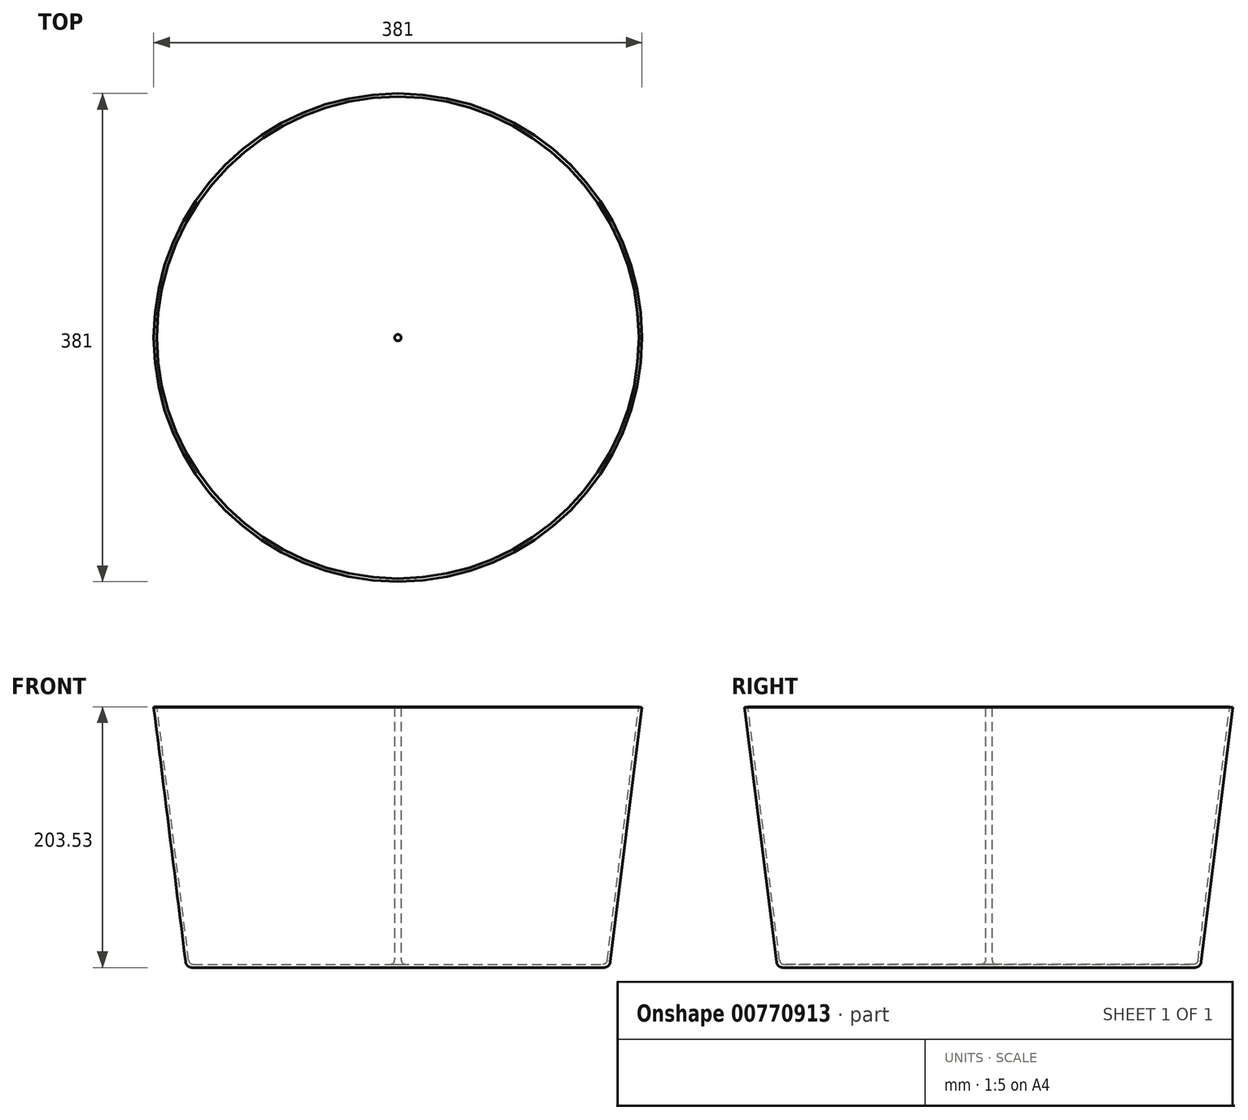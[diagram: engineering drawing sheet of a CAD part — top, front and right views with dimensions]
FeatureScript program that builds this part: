
annotation { "Feature Type Name" : "Feature", "Feature Type Description" : "" }
export const myFeature = defineFeature(function(context is Context, id is Id, definition is map)
    precondition{}
    {
        {
            var Q0;
            Q0=qCreatedBy(makeId("Front.planeOp"),FACE);
            var sketch = newSketch(context, id + "F0", { "sketchPlane" : qUnion([Q0])});
            skLineSegment(sketch, "E0", {"start": v(0, 0) * mm, "end": v(160.73, 0) * mm});
            skLineSegment(sketch, "E1", {"start": v(0, 0) * mm, "end": v(0, 203.21) * mm});
            skLineSegment(sketch, "E2", {"start": v(165.64, 4.34) * mm, "end": v(190.5, 203.21) * mm});
            skLineSegment(sketch, "E3.0", {"start": v(163.23, 5.54) * mm, "end": v(187.98, 203.53) * mm});
            skLineSegment(sketch, "E3.1", {"start": v(5.97, 2.54) * mm, "end": v(159.83, 2.54) * mm});
            skLineSegment(sketch, "E3.2", {"start": v(2.54, 5.97) * mm, "end": v(2.54, 203.21) * mm});
            skPoint(sketch, "E4.visualSharp", {"position": v(165.1, 0) * mm});
            skArc(sketch, "E4.filletArc", {"start": v(160.73, 0) * mm, "mid": v(164, 1.24) * mm, "end": v(165.64, 4.34) * mm});
            skArc(sketch, "E5.filletArc", {"start": v(159.83, 2.54) * mm, "mid": v(162.1, 3.4) * mm, "end": v(163.23, 5.54) * mm});
            skPoint(sketch, "E6.visualSharp", {"position": v(2.54, 2.54) * mm});
            skArc(sketch, "E6.filletArc", {"start": v(2.54, 5.97) * mm, "mid": v(3.54, 3.54) * mm, "end": v(5.97, 2.54) * mm});
            skLineSegment(sketch, "E7", {"start": v(0, 203.21) * mm, "end": v(2.54, 203.21) * mm});
            skLineSegment(sketch, "E8", {"start": v(187.98, 203.53) * mm, "end": v(190.5, 203.21) * mm});
            skLineSegment(sketch, "E9", {"start": v(187.98, 203.53) * mm, "end": v(2.54, 203.21) * mm});
            skSolve(sketch);
        }
        {
            var Q0;
            Q0=makeQuery(id+"F0.imprint","IMPRINT",FACE,{"disambiguationData":[TD([[makeQuery(id+"F0.imprint","IMPRINT",EDGE,{"derivedFrom":sQuery(id+"F0.wireOp",EDGE,"E0")}),1.0]])]});
            var Q1;
            Q1=sQuery(id+"F0.wireOp",EDGE,"E1");
            revolve(context, id + "F1", {"surfaceOperationType" : NewSurfaceOperationType.NEW, "entities" : qUnion([Q0]), "axis" : qUnion([Q1]), "revolveType" : RevolveType.FULL});
        }
        {
            var Q0;
            Q0=qCreatedBy(makeId("Top.planeOp"),FACE);
            var sketch = newSketch(context, id + "F2", { "sketchPlane" : qUnion([Q0])});
            skCircle(sketch, "E10.0", {"center": v(0, 0) * mm, "radius": 154.38 * mm});
            skLineSegment(sketch, "E11.0", {"start": v(-2.54, -5.97) * mm, "end": v(-2.54, -162.56) * mm});
            skLineSegment(sketch, "E12.0", {"start": v(2.54, -5.97) * mm, "end": v(2.54, -162.56) * mm});
            skLineSegment(sketch, "E13.0", {"start": v(-5.97, -2.54) * mm, "end": v(-162.56, -2.54) * mm});
            skPoint(sketch, "E14.newPointA", {"position": v(0, -2.54) * mm});
            skArc(sketch, "E14.filletArc", {"start": v(-2.54, -5.97) * mm, "mid": v(-3.54, -3.54) * mm, "end": v(-5.97, -2.54) * mm});
            skLineSegment(sketch, "E15.MirrorCS", {"start": v(5.97, -2.54) * mm, "end": v(162.56, -2.54) * mm});
            skArc(sketch, "E16.MirrorCS", {"start": v(2.54, -5.97) * mm, "mid": v(3.54, -3.54) * mm, "end": v(5.97, -2.54) * mm});
            skLineSegment(sketch, "E17.MirrorCS", {"start": v(-5.97, 2.54) * mm, "end": v(-162.56, 2.54) * mm});
            skLineSegment(sketch, "E18.MirrorCS", {"start": v(-2.54, 5.97) * mm, "end": v(-2.54, 162.56) * mm});
            skArc(sketch, "E19.MirrorCS", {"start": v(-2.54, 5.97) * mm, "mid": v(-3.54, 3.54) * mm, "end": v(-5.97, 2.54) * mm});
            skLineSegment(sketch, "E20.MirrorCS", {"start": v(5.97, 2.54) * mm, "end": v(162.56, 2.54) * mm});
            skArc(sketch, "E21.MirrorCS", {"start": v(2.54, 5.97) * mm, "mid": v(3.54, 3.54) * mm, "end": v(5.97, 2.54) * mm});
            skLineSegment(sketch, "E22.MirrorCS", {"start": v(2.54, 5.97) * mm, "end": v(2.54, 162.56) * mm});
            skPoint(sketch, "E23.orphan", {"position": v(2.54, 0) * mm});
            skSolve(sketch);
        }
        {
            var Q0;
            Q0=qCreatedBy(makeId("Top.planeOp"),FACE);
            cPlane(context, id + "F3", {"entities" : qUnion([Q0]), "cplaneType" : CPlaneType.OFFSET, "offset" : 203.2 * mm, "width" : 152.4 * mm, "height" : 152.4 * mm});
        }
    });
